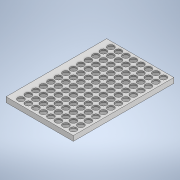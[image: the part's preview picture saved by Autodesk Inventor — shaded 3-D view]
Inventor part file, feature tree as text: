
AUTODESK INVENTOR PART (.ipt)
format: ipt  version: 2020 (Build 240168000, 168)  size: 281,600 bytes
history: native  units: in
note: dims shown in document units (in); Inventor stores cm internally (conversion verified against a paired STEP export)
features: sketch x2, extrude x1, hole x1, pattern_linear x1
ambient origin geometry x8: Origin, YZ Plane, XZ Plane, XY Plane, X Axis, Y Axis, Z Axis, Center Point
bodies: Solid1 (feature_tree)
feature tree (5):
  extrude  "Extrusion1"  Depth=5.0299in
  hole  "Hole1"  [1 undecoded]
  pattern_linear  "Rectangular Pattern1"  Spacing1=0.25in  [1 undecoded]
  sketch  "Sketch1"  dims[d0=3.3654in d1=5.0299in]
  sketch  "Sketch2"  dims[d3=45.0deg d4=0.375in d5=0.25in d6=0.0in d7=0.375in d8=135.0deg d9=0.375in d10=0.3125in d11=0.75in d12=0.332in d13=0.25in d14=0.5635in d15=0.0625in d16=0.8108in d17=3.1496in d19=0.375in d20=5.1181in d22=0.375in]
note: 2 required parameter values undecoded (feature->parameter linkage not recoverable at this tier; creation-order binding heuristic only, values carry confidence <= 0.55)
